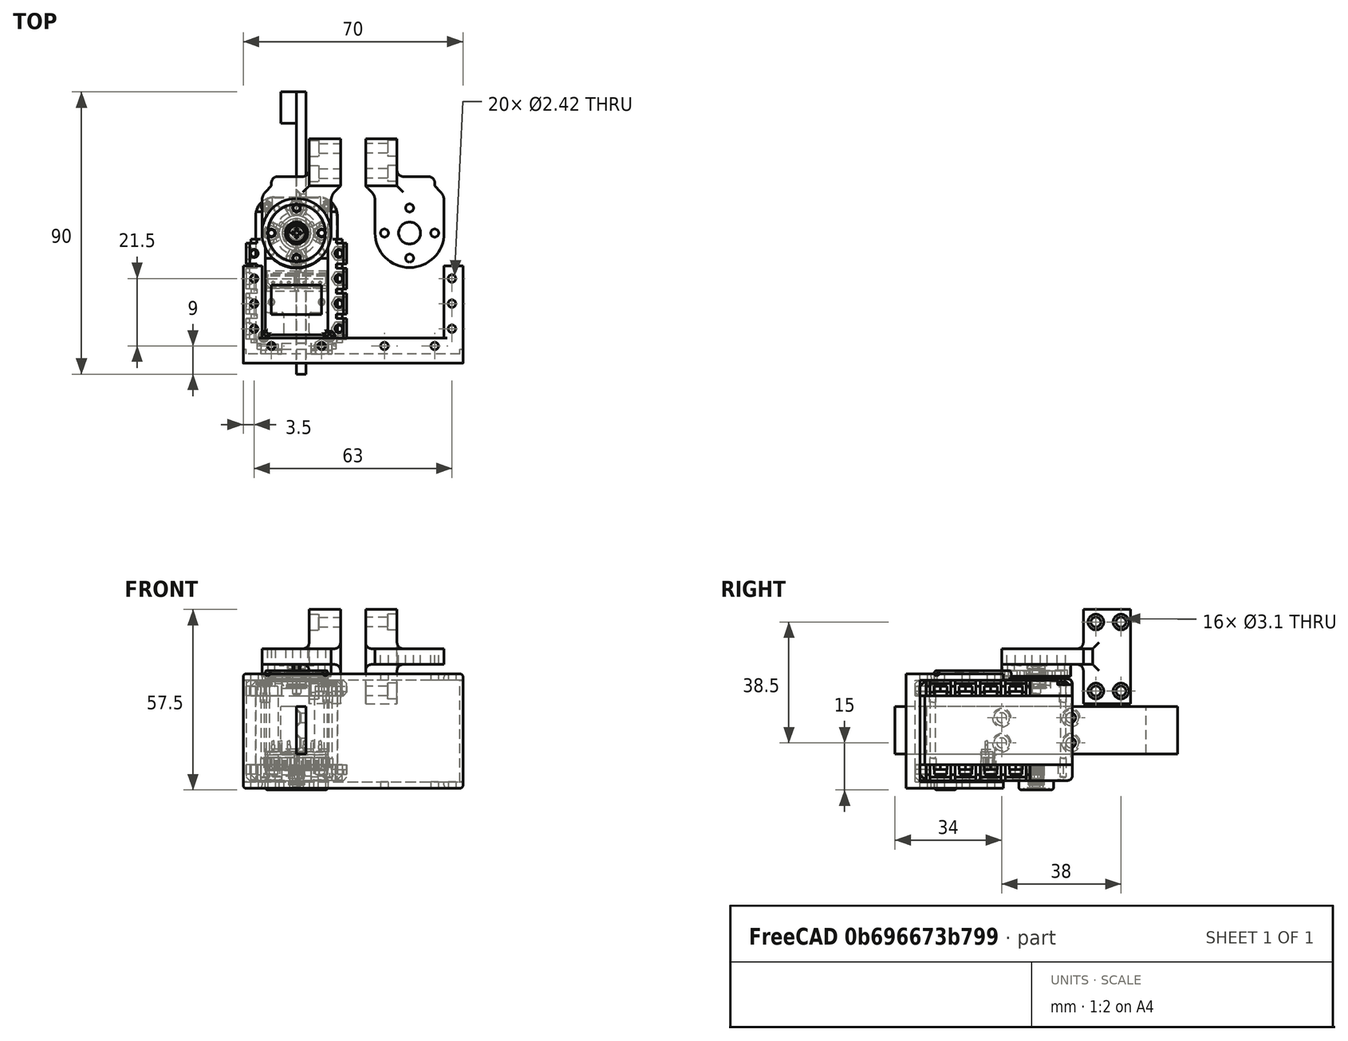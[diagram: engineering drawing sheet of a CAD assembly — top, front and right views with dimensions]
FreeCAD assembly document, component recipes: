
FREECAD ASSEMBLY — COMPONENT RECIPES ("Unnamed")

This assembly document has 8 components, labeled P0..P7 below (a component is one placed body or linked part). 6 of them carry a construction recipe — the FreeCAD feature program that regenerates the part from scratch, quoted from this document or its linked companion documents; the rest are supplied as boundary geometry only. No exploded tour is included for this assembly.
COMPONENT P0 — geometry summary ("ASM0001_ASM002"; no construction recipe available for this part):
  bounding box: 50.0 x 40.0 x 32.0 mm
  tessellated surface: 148,570 triangles
  volume: 42792 mm^3 (67% of its bounding box)
COMPONENT P1 — geometry summary ("ASM0001_ASM003"; no construction recipe available for this part):
  bounding box: 50.0 x 40.0 x 32.0 mm
  tessellated surface: 148,570 triangles
  volume: 42792 mm^3 (67% of its bounding box)
COMPONENT P2 — recipe-attached ("Body006", modeled in this document).
Construction recipe (the document's own serialized feature program — sketch geometry with constraints, then the solid features built on it; lengths are millimeters unless a unit is written):

FEATURE [PartDesign::ShapeBinder] CopyPart__Feature
  TraceSupport = false
FEATURE [Sketcher::SketchObject] Sketch012
  ArcFitTolerance = 1e-06
  AttachmentSupport = -> [CopyPart__Feature]
  ExternalTypes = [0]
  FullyConstrained = true
  MakeInternals = false
  MapMode = 5
  Placement = pos=(0,-38.5,0) rot=(1,0,0;1.5708rad)
  _ExternalGeoVersion = 1
  sketch-geometry (4):
    g0: LineSegment StartX=-17 StartY=18 StartZ=0 EndX=-17 EndY=-18.5 EndZ=0
    g1: LineSegment StartX=-17 StartY=-18.5 StartZ=0 EndX=53 EndY=-18.5 EndZ=0
    g2: LineSegment StartX=53 StartY=-18.5 StartZ=0 EndX=53 EndY=18 EndZ=0
    g3: LineSegment StartX=53 StartY=18 StartZ=0 EndX=-17 EndY=18 EndZ=0
  constraints (12):
    c: Coincident(g0,g1)
    c: Coincident(g1,g2)
    c: Coincident(g2,g3)
    c: Coincident(g3,g0)
    c: Vertical(g0)
    c: Vertical(g2)
    c: Horizontal(g1)
    c: Horizontal(g3)
    c: DistanceY(g0,g0) = 36.5
    c: Distance(g-2,g0) = 17
    c: DistanceX(g1,g1) = 70
    c: Distance(g-1,g3) = 18
FEATURE [PartDesign::Pad] Pad006
  Direction = (0,-1,2e-16)
  Length = 3
  Length2 = 10
  Profile = -> Sketch012
  ReferenceAxis = -> Sketch012 [N_Axis]
  Refine = true
  SideType = 0
  Suppressed = false
  Type = 0
  Type2 = 0
FEATURE [Sketcher::SketchObject] Sketch013
  ArcFitTolerance = 1e-06
  AttachmentSupport = -> [Pad006]
  ExternalTypes = [0]
  FullyConstrained = true
  MakeInternals = false
  MapMode = 5
  Placement = pos=(0,-38.5,1.5e-14) rot=(0,0.707107,0.707107;3.14159rad)
  _ExternalGeoVersion = 1
  sketch-geometry (4):
    g0: LineSegment StartX=17 StartY=18 StartZ=0 EndX=-53 EndY=18 EndZ=0
    g1: LineSegment StartX=-53 StartY=18 StartZ=0 EndX=-53 EndY=16 EndZ=0
    g2: LineSegment StartX=-53 StartY=16 StartZ=0 EndX=17 EndY=16 EndZ=0
    g3: LineSegment StartX=17 StartY=16 StartZ=0 EndX=17 EndY=18 EndZ=0
  constraints (12):
    c: Coincident(g0,g1)
    c: Coincident(g1,g2)
    c: Coincident(g2,g3)
    c: Coincident(g3,g0)
    c: Horizontal(g0)
    c: Horizontal(g2)
    c: Vertical(g1)
    c: Vertical(g3)
    c: Distance(g1,g3) = 70
    c: Distance(g0,g2) = 2
    c: Distance(g-1,g2) = 16
    c: Distance(g-2,g3) = 17
FEATURE [PartDesign::Pad] Pad007
  BaseFeature = -> Pad006
  Direction = (0,1,-2e-16)
  Length = 5
  Length2 = 10
  Profile = -> Sketch013
  ReferenceAxis = -> Sketch013 [N_Axis]
  Refine = true
  SideType = 0
  Suppressed = false
  Type = 0
  Type2 = 0
FEATURE [Sketcher::SketchObject] Sketch014
  ArcFitTolerance = 1e-06
  AttachmentSupport = -> [Pad007]
  ExternalTypes = [0]
  FullyConstrained = true
  MakeInternals = false
  MapMode = 5
  Placement = pos=(0,-38.5,1.5e-14) rot=(0,0.707107,0.707107;3.14159rad)
  _ExternalGeoVersion = 1
  sketch-geometry (4):
    g0: LineSegment StartX=17 StartY=-18.5 StartZ=0 EndX=17 EndY=-16.5 EndZ=0
    g1: LineSegment StartX=17 StartY=-16.5 StartZ=0 EndX=-53 EndY=-16.5 EndZ=0
    g2: LineSegment StartX=-53 StartY=-16.5 StartZ=0 EndX=-53 EndY=-18.5 EndZ=0
    g3: LineSegment StartX=-53 StartY=-18.5 StartZ=0 EndX=17 EndY=-18.5 EndZ=0
  constraints (12):
    c: Coincident(g0,g1)
    c: Coincident(g1,g2)
    c: Coincident(g2,g3)
    c: Coincident(g3,g0)
    c: Vertical(g0)
    c: Vertical(g2)
    c: Horizontal(g1)
    c: Horizontal(g3)
    c: Distance(g0,g2) = 70
    c: Distance(g1,g3) = 2
    c: Distance(g-2,g0) = 17
    c: Distance(g-1,g3) = 18.5
FEATURE [PartDesign::Pad] Pad008
  BaseFeature = -> Pad007
  Direction = (0,1,-2e-16)
  Length = 5
  Length2 = 10
  Profile = -> Sketch014
  ReferenceAxis = -> Sketch014 [N_Axis]
  Refine = true
  SideType = 0
  Suppressed = false
  Type = 0
  Type2 = 0
FEATURE [Sketcher::SketchObject] Sketch015
  ArcFitTolerance = 1e-06
  AttachmentSupport = -> [Pad008]
  ExternalTypes = [0,0]
  FullyConstrained = true
  MakeInternals = false
  MapMode = 5
  Placement = pos=(0,-33.5,1.19e-13) rot=(0,0.707107,0.707107;3.14159rad)
  _ExternalGeoVersion = 1
  sketch-geometry (16):
    g0: LineSegment StartX=17 StartY=16 StartZ=0 EndX=17 EndY=18 EndZ=0
    g1: LineSegment StartX=17 StartY=18 StartZ=0 EndX=11 EndY=18 EndZ=0
    g2: LineSegment StartX=11 StartY=18 StartZ=0 EndX=11 EndY=16 EndZ=0
    g3: LineSegment StartX=11 StartY=16 StartZ=0 EndX=17 EndY=16 EndZ=0
    g4: LineSegment StartX=-53 StartY=16 StartZ=0 EndX=-47 EndY=16 EndZ=0
    g5: LineSegment StartX=-47 StartY=16 StartZ=0 EndX=-47 EndY=18 EndZ=0
    g6: LineSegment StartX=-47 StartY=18 StartZ=0 EndX=-53 EndY=18 EndZ=0
    g7: LineSegment StartX=-53 StartY=18 StartZ=0 EndX=-53 EndY=16 EndZ=0
    g8: LineSegment StartX=-53 StartY=-16.5 StartZ=0 EndX=-53 EndY=-18.5 EndZ=0
    g9: LineSegment StartX=-53 StartY=-18.5 StartZ=0 EndX=-47 EndY=-18.5 EndZ=0
    g10: LineSegment StartX=-47 StartY=-18.5 StartZ=0 EndX=-47 EndY=-16.5 EndZ=0
    g11: LineSegment StartX=-47 StartY=-16.5 StartZ=0 EndX=-53 EndY=-16.5 EndZ=0
    g12: LineSegment StartX=17 StartY=-16.5 StartZ=0 EndX=11 EndY=-16.5 EndZ=0
    g13: LineSegment StartX=11 StartY=-16.5 StartZ=0 EndX=11 EndY=-18.5 EndZ=0
    g14: LineSegment StartX=11 StartY=-18.5 StartZ=0 EndX=17 EndY=-18.5 EndZ=0
    g15: LineSegment StartX=17 StartY=-18.5 StartZ=0 EndX=17 EndY=-16.5 EndZ=0
  constraints (48):
    c: Coincident(g0,g1)
    c: Coincident(g1,g2)
    c: Coincident(g2,g3)
    c: Coincident(g3,g0)
    c: Vertical(g0)
    c: Vertical(g2)
    c: Horizontal(g1)
    c: Horizontal(g3)
    c: Distance(g0,g2) = 6
    c: Distance(g1,g3) = 2
    c: Distance(g-1,g3) = 16
    c: Distance(g-2,g0) = 17
    c: Coincident(g4,g5)
    c: Coincident(g5,g6)
    c: Coincident(g6,g7)
    c: Coincident(g7,g4)
    c: Horizontal(g4)
    c: Horizontal(g6)
    c: Vertical(g5)
    c: Vertical(g7)
    c: Distance(g-1,g4) = 16
    c: Distance(g7,g7) = 2
    c: Distance(g-2,g7) = 53
    c: Distance(g6,g6) = 6
    c: Coincident(g8,g9)
    c: Coincident(g9,g10)
    c: Coincident(g10,g11)
    c: Coincident(g11,g8)
    c: Vertical(g8)
    c: Vertical(g10)
    c: Horizontal(g9)
    c: Horizontal(g11)
    c: Coincident(g12,g13)
    c: Coincident(g13,g14)
    c: Coincident(g14,g15)
    c: Coincident(g15,g12)
    c: Horizontal(g12)
    c: Horizontal(g14)
    c: Vertical(g13)
    c: Vertical(g15)
    c: Distance(g-2,g15) = 17
    c: Distance(g-1,g12) = 16.5
    c: Distance(g13,g13) = 2
    c: Distance(g14,g14) = 6
    c: Distance(g-1,g11) = 16.5
    c: Distance(g-2,g8) = 53
    c: Distance(g9,g9) = 6
    c: Distance(g10,g10) = 2
FEATURE [PartDesign::Pad] Pad009
  BaseFeature = -> Pad008
  Direction = (0,1,-3.6e-15)
  Length = 23
  Length2 = 10
  Profile = -> Sketch015
  ReferenceAxis = -> Sketch015 [N_Axis]
  Refine = true
  SideType = 0
  Suppressed = false
  Type = 0
  Type2 = 0
FEATURE [Sketcher::SketchObject] Sketch016
  ArcFitTolerance = 1e-06
  AttachmentSupport = -> [Pad009]
  ExternalTypes = [0,0]
  FullyConstrained = true
  MakeInternals = false
  MapMode = 5
  Placement = pos=(0,-38.5,1.5e-14) rot=(0,0.707107,0.707107;3.14159rad)
  _ExternalGeoVersion = 1
  sketch-geometry (8):
    g0: LineSegment StartX=-53 StartY=16 StartZ=0 EndX=-53 EndY=-16.5 EndZ=0
    g1: LineSegment StartX=-53 StartY=-16.5 StartZ=0 EndX=-52 EndY=-16.5 EndZ=0
    g2: LineSegment StartX=-52 StartY=-16.5 StartZ=0 EndX=-52 EndY=16 EndZ=0
    g3: LineSegment StartX=-52 StartY=16 StartZ=0 EndX=-53 EndY=16 EndZ=0
    g4: LineSegment StartX=17 StartY=16 StartZ=0 EndX=16 EndY=16 EndZ=0
    g5: LineSegment StartX=16 StartY=16 StartZ=0 EndX=16 EndY=-16.5 EndZ=0
    g6: LineSegment StartX=16 StartY=-16.5 StartZ=0 EndX=17 EndY=-16.5 EndZ=0
    g7: LineSegment StartX=17 StartY=-16.5 StartZ=0 EndX=17 EndY=16 EndZ=0
  constraints (24):
    c: Coincident(g0,g1)
    c: Coincident(g1,g2)
    c: Coincident(g2,g3)
    c: Coincident(g3,g0)
    c: Vertical(g0)
    c: Vertical(g2)
    c: Horizontal(g1)
    c: Horizontal(g3)
    c: Distance(g0,g2) = 1
    c: Distance(g1,g3) = 32.5
    c: Distance(g-1,g3) = 16
    c: Distance(g-2,g0) = 53
    c: Coincident(g4,g5)
    c: Coincident(g5,g6)
    c: Coincident(g6,g7)
    c: Coincident(g7,g4)
    c: Horizontal(g4)
    c: Horizontal(g6)
    c: Vertical(g5)
    c: Vertical(g7)
    c: Distance(g-2,g7) = 17
    c: Distance(g-1,g4) = 16
    c: Distance(g7,g7) = 32.5
    c: Distance(g6,g6) = 1
FEATURE [PartDesign::Pad] Pad010
  BaseFeature = -> Pad009
  Direction = (0,1,-2e-16)
  Length = 1.5
  Length2 = 10
  Profile = -> Sketch016
  ReferenceAxis = -> Sketch016 [N_Axis]
  Refine = true
  SideType = 0
  Suppressed = false
  Type = 0
  Type2 = 0
FEATURE [PartDesign::Fillet] Fillet008
  Base = -> Pad010 [Edge47,Edge45,Edge20,Edge18,Edge5,Edge23,Edge41,Edge43]
  BaseFeature = -> Pad010
  Radius = 1
  Refine = true
  SupportTransform = false
  Suppressed = false
  UseAllEdges = false
FEATURE [Sketcher::SketchObject] Sketch017
  ArcFitTolerance = 1e-06
  AttachmentSupport = -> [Fillet008]
  ExternalTypes = [0]
  FullyConstrained = true
  MakeInternals = false
  MapMode = 5
  Placement = pos=(0,-1.22e-14,18) rot=(0,0,1;0rad)
  _ExternalGeoVersion = 1
  sketch-geometry (10):
    g0: Circle CenterX=-13.5 CenterY=-14.5 CenterZ=0 NormalX=0 NormalY=0 NormalZ=1 AngleXU=0 Radius=1.1
    g1: Circle CenterX=-13.5 CenterY=-22.5 CenterZ=0 NormalX=0 NormalY=0 NormalZ=1 AngleXU=0 Radius=1.1
    g2: Circle CenterX=-13.5 CenterY=-30.5 CenterZ=0 NormalX=0 NormalY=0 NormalZ=1 AngleXU=0 Radius=1.1
    g3: Circle CenterX=49.5 CenterY=-14.5 CenterZ=0 NormalX=0 NormalY=0 NormalZ=1 AngleXU=0 Radius=1.1
    g4: Circle CenterX=49.5 CenterY=-22.5 CenterZ=0 NormalX=0 NormalY=0 NormalZ=1 AngleXU=0 Radius=1.1
    g5: Circle CenterX=49.5 CenterY=-30.5 CenterZ=0 NormalX=0 NormalY=0 NormalZ=1 AngleXU=0 Radius=1.1
    g6: Circle CenterX=-8 CenterY=-36 CenterZ=0 NormalX=0 NormalY=0 NormalZ=1 AngleXU=0 Radius=1.1
    g7: Circle CenterX=8 CenterY=-36 CenterZ=0 NormalX=0 NormalY=0 NormalZ=1 AngleXU=0 Radius=1.1
    g8: Circle CenterX=44 CenterY=-36 CenterZ=0 NormalX=0 NormalY=0 NormalZ=1 AngleXU=0 Radius=1.1
    g9: Circle CenterX=28 CenterY=-36 CenterZ=0 NormalX=0 NormalY=0 NormalZ=1 AngleXU=0 Radius=1.1
  constraints (30):
    c: Diameter(g0) = 2.2
    c: Equal(g0,g1)
    c: Equal(g2,g1)
    c: Distance(g0,g-2) = 13.5
    c: DistanceY(g0,g-1) = 14.5
    c: Distance(g1,g0) = 8
    c: Distance(g1,g-2) = 13.5
    c: Distance(g2,g1) = 8
    c: Distance(g2,g-2) = 13.5
    c: Diameter(g3) = 2.2
    c: DistanceX(g-1,g3) = 49.5
    c: DistanceY(g3,g-1) = 14.5
    c: Equal(g3,g4)
    c: Equal(g4,g5)
    c: Distance(g4,g3) = 8
    c: Distance(g5,g4) = 8
    c: Distance(g4,g-2) = 49.5
    c: Distance(g5,g-2) = 49.5
    c: Equal(g2,g6)
    c: Distance(g6,g-2) = 8
    c: DistanceY(g6,g-1) = 36
    c: Equal(g7,g6)
    c: DistanceX(g6,g7) = 16
    c: Distance(g7,g-1) = 36
    c: Equal(g9,g5)
    c: Equal(g8,g5)
    c: DistanceX(g9,g8) = 16
    c: Distance(g9,g-1) = 36
    c: Distance(g8,g-1) = 36
    c: Distance(g9,g-2) = 28
FEATURE [PartDesign::Hole] Hole006
  BaseFeature = -> Fillet008
  BaseProfileType = 7
  CustomThreadClearance = 0
  Depth = 40
  DepthType = 0
  Diameter = 2.42
  DrillForDepth = false
  DrillPoint = 1
  DrillPointAngle = 118
  HoleCutCountersinkAngle = 90
  HoleCutCustomValues = false
  HoleCutDepth = 0
  HoleCutDiameter = 0
  HoleCutType = 0
  ModelThread = false
  Profile = -> Sketch017
  Refine = true
  Suppressed = false
  Tapered = false
  TaperedAngle = 90
  ThreadClass = 0
  ThreadDepth = 40
  ThreadDepthType = 0
  ThreadDiameter = 2.2
  ThreadDirection = 0
  ThreadFit = 0
  ThreadSize = 7
  ThreadType = 1
  Threaded = false
  UseCustomThreadClearance = false
FEATURE [PartDesign::Body] Body002
  AllowCompound = true
  Group = -> [CopyPart__Feature,Sketch012,Pad006,Sketch013,Pad007,Sketch014,Pad008,Sketch015,Pad009,Sketch016,Pad010,Fillet008,Sketch017,Hole006]
  Origin = -> Origin012
  Tip = -> Hole006
COMPONENT P3 — recipe-attached ("Body007", modeled in this document).
Construction recipe (the document's own serialized feature program — sketch geometry with constraints, then the solid features built on it; lengths are millimeters unless a unit is written):

FEATURE [PartDesign::ShapeBinder] CopyPart__Feature009
  Placement = pos=(0,0,19.16) rot=(0,0,1;1.5708rad)
  TraceSupport = false
FEATURE [Sketcher::SketchObject] Sketch
  ArcFitTolerance = 1e-06
  AttachmentSupport = -> [CopyPart__Feature009]
  ExternalTypes = [0]
  FullyConstrained = true
  MakeInternals = false
  MapMode = 5
  Placement = pos=(0,0,21) rot=(0,0,1;1.5708rad)
  _ExternalGeoVersion = 1
  sketch-geometry (4):
    g0: LineSegment StartX=-2e-15 StartY=-11 StartZ=0 EndX=12 EndY=-11 EndZ=0
    g1: LineSegment StartX=12 StartY=-11 StartZ=0 EndX=12 EndY=11 EndZ=0
    g2: LineSegment StartX=12 StartY=11 StartZ=0 EndX=-3.6e-15 EndY=11 EndZ=0
    g3: ArcOfCircle CenterX=0 CenterY=5e-16 CenterZ=0 NormalX=0 NormalY=0 NormalZ=1 AngleXU=0 Radius=11 StartAngle=1.5708 EndAngle=4.71239
  constraints (12):
    c: Coincident(g0,g1)
    c: Coincident(g1,g2)
    c: Horizontal(g0)
    c: Horizontal(g2)
    c: Vertical(g1)
    c: Distance(g1,g0) = 12
    c: Distance(g0,g2) = 22
    c: PointOnObject(g0,g-2)
    c: Distance(g-1,g0) = 11
    c: Tangent(g0,g3) = -1.5708
    c: Coincident(g3,g2)
    c: Angle(g3) = 3.14159
FEATURE [PartDesign::Pad] Pad
  Direction = (0,0,1)
  Length = 5
  Length2 = 10
  Placement = pos=(0,0,19.16) rot=(0,0,1;1.5708rad)
  Profile = -> Sketch
  ReferenceAxis = -> Sketch [N_Axis]
  Refine = true
  SideType = 0
  Suppressed = false
  Type = 0
  Type2 = 0
FEATURE [Sketcher::SketchObject] Sketch001
  ArcFitTolerance = 1e-06
  AttachmentSupport = -> [Pad]
  ExternalTypes = [0]
  FullyConstrained = true
  MakeInternals = false
  MapMode = 5
  Placement = pos=(0,0,26) rot=(0,0,1;1.5708rad)
  _ExternalGeoVersion = 1
  sketch-geometry (1):
    g0: Circle CenterX=-8 CenterY=0 CenterZ=0 NormalX=0 NormalY=0 NormalZ=1 AngleXU=0 Radius=1.1
  constraints (3):
    c: Diameter(g0) = 2.2
    c: PointOnObject(g0,g-1)
    c: Distance(g0,g-2) = 8
FEATURE [PartDesign::Hole] Hole
  BaseFeature = -> Pad
  BaseProfileType = 7
  CustomThreadClearance = 0
  Depth = 5
  DepthType = 0
  Diameter = 2.552
  DrillForDepth = false
  DrillPoint = 1
  DrillPointAngle = 118
  HoleCutCountersinkAngle = 90
  HoleCutCustomValues = false
  HoleCutDepth = 0
  HoleCutDiameter = 0
  HoleCutType = 0
  ModelThread = false
  Placement = pos=(0,0,19.16) rot=(0,0,1;1.5708rad)
  Profile = -> Sketch001
  Refine = true
  Suppressed = false
  Tapered = false
  TaperedAngle = 90
  ThreadClass = 0
  ThreadDepth = 5
  ThreadDepthType = 0
  ThreadDiameter = 2.2
  ThreadDirection = 0
  ThreadFit = 2
  ThreadSize = 7
  ThreadType = 1
  Threaded = false
  UseCustomThreadClearance = false
FEATURE [PartDesign::PolarPattern] PolarPattern
  Angle = 360
  Axis = -> Sketch001 [N_Axis]
  BaseFeature = -> Hole
  Mode = 0
  Occurrences = 4
  Offset = 120
  Originals = -> [Hole]
  Placement = pos=(0,0,19.16) rot=(0,0,1;1.5708rad)
  Refine = true
  SpacingPattern = [0]
  Spacings = [-1,-1,-1]
  Suppressed = false
  TransformMode = 0
FEATURE [Sketcher::SketchObject] Sketch002
  ArcFitTolerance = 1e-06
  AttachmentSupport = -> [PolarPattern]
  ExternalTypes = [0]
  FullyConstrained = true
  MakeInternals = false
  MapMode = 5
  Placement = pos=(0,0,26) rot=(0,0,1;1.5708rad)
  _ExternalGeoVersion = 1
  sketch-geometry (1):
    g0: Circle CenterX=0 CenterY=0 CenterZ=0 NormalX=0 NormalY=0 NormalZ=1 AngleXU=0 Radius=3
  constraints (2):
    c: Diameter(g0) = 6
    c: Coincident(g0,g-1)
FEATURE [PartDesign::Hole] Hole001
  BaseFeature = -> PolarPattern
  BaseProfileType = 7
  CustomThreadClearance = 0
  Depth = 5
  DepthType = 0
  Diameter = 7
  DrillForDepth = false
  DrillPoint = 1
  DrillPointAngle = 118
  HoleCutCountersinkAngle = 90
  HoleCutCustomValues = false
  HoleCutDepth = 0
  HoleCutDiameter = 0
  HoleCutType = 0
  ModelThread = false
  Placement = pos=(0,0,19.16) rot=(0,0,1;1.5708rad)
  Profile = -> Sketch002
  Refine = true
  Suppressed = false
  Tapered = false
  TaperedAngle = 90
  ThreadClass = 0
  ThreadDepth = 5
  ThreadDepthType = 0
  ThreadDiameter = 6
  ThreadDirection = 0
  ThreadFit = 2
  ThreadSize = 14
  ThreadType = 1
  Threaded = false
  UseCustomThreadClearance = false
FEATURE [Sketcher::SketchObject] Sketch018
  ArcFitTolerance = 1e-06
  AttachmentSupport = -> [Hole001]
  ExternalTypes = [0]
  FullyConstrained = true
  MakeInternals = false
  MapMode = 5
  Placement = pos=(0,0,26) rot=(0,0,1;1.5708rad)
  _ExternalGeoVersion = 1
  sketch-geometry (4):
    g0: LineSegment StartX=12 StartY=11 StartZ=0 EndX=15 EndY=8.00374 EndZ=0
    g1: LineSegment StartX=15 StartY=8.00374 StartZ=0 EndX=15 EndY=-13.9963 EndZ=0
    g2: LineSegment StartX=15 StartY=-13.9963 StartZ=0 EndX=12 EndY=-11 EndZ=0
    g3: LineSegment StartX=12 StartY=11 StartZ=0 EndX=12 EndY=-11 EndZ=0
  constraints (12):
    c: Coincident(g0,g1)
    c: Vertical(g1)
    c: Coincident(g1,g2)
    c: Coincident(g0,g3)
    c: Coincident(g3,g2)
    c: Vertical(g3)
    c: Distance(g1,g1) = 22
    c: Distance(g0,g0) = 4.24
    c: Equal(g1,g3)
    c: Distance(g-2,g1) = 15
    c: Distance(g-2,g3) = 12
    c: Distance(g0,g-1) = 11
FEATURE [PartDesign::Pad] Pad011
  BaseFeature = -> Hole001
  Direction = (0,0,1)
  Length = 5
  Length2 = 10
  Placement = pos=(0,0,19.16) rot=(0,0,1;1.5708rad)
  Profile = -> Sketch018
  ReferenceAxis = -> Sketch018 [N_Axis]
  Refine = true
  Reversed = true
  SideType = 0
  Suppressed = false
  Type = 0
  Type2 = 0
FEATURE [Sketcher::SketchObject] Sketch019
  ArcFitTolerance = 1e-06
  AttachmentSupport = -> [Pad011]
  ExternalTypes = [0,0,0]
  FullyConstrained = true
  MakeInternals = false
  MapMode = 5
  Placement = pos=(0,0,26) rot=(0,0,1;1.5708rad)
  _ExternalGeoVersion = 1
  sketch-geometry (4):
    g0: LineSegment StartX=15 StartY=8 StartZ=0 EndX=15 EndY=-14 EndZ=0
    g1: LineSegment StartX=15 StartY=-14 StartZ=0 EndX=18 EndY=-14 EndZ=0
    g2: LineSegment StartX=18 StartY=-14 StartZ=0 EndX=18 EndY=8 EndZ=0
    g3: LineSegment StartX=18 StartY=8 StartZ=0 EndX=15 EndY=8 EndZ=0
  constraints (12):
    c: Coincident(g0,g1)
    c: Coincident(g1,g2)
    c: Coincident(g2,g3)
    c: Coincident(g3,g0)
    c: Vertical(g0)
    c: Vertical(g2)
    c: Horizontal(g1)
    c: Horizontal(g3)
    c: Distance(g0,g2) = 3
    c: Distance(g1,g3) = 22
    c: Distance(g-2,g2) = 18
    c: Distance(g1,g-1) = 14
FEATURE [PartDesign::Pad] Pad012
  BaseFeature = -> Pad011
  Direction = (0,0,1)
  Length = 5
  Length2 = 10
  Placement = pos=(0,0,19.16) rot=(0,0,1;1.5708rad)
  Profile = -> Sketch019
  ReferenceAxis = -> Sketch019 [N_Axis]
  Refine = true
  Reversed = true
  SideType = 0
  Suppressed = false
  Type = 0
  Type2 = 0
FEATURE [Sketcher::SketchObject] Sketch020
  ArcFitTolerance = 1e-06
  AttachmentSupport = -> [Pad012]
  ExternalTypes = [0]
  FullyConstrained = true
  MakeInternals = false
  MapMode = 5
  Placement = pos=(14,-4.7e-15,19.16) rot=(0.57735,0.57735,0.57735;2.0944rad)
  _ExternalGeoVersion = 1
  sketch-geometry (4):
    g0: LineSegment StartX=15 StartY=19.34 StartZ=0 EndX=15 EndY=-10.66 EndZ=0
    g1: LineSegment StartX=15 StartY=-10.66 StartZ=0 EndX=30 EndY=-10.66 EndZ=0
    g2: LineSegment StartX=30 StartY=-10.66 StartZ=0 EndX=30 EndY=19.34 EndZ=0
    g3: LineSegment StartX=30 StartY=19.34 StartZ=0 EndX=15 EndY=19.34 EndZ=0
  constraints (12):
    c: Coincident(g0,g1)
    c: Coincident(g1,g2)
    c: Coincident(g2,g3)
    c: Coincident(g3,g0)
    c: Vertical(g0)
    c: Vertical(g2)
    c: Horizontal(g1)
    c: Horizontal(g3)
    c: Distance(g0,g2) = 15
    c: Distance(g1,g3) = 30
    c: Distance(g-1,g1) = 10.66
    c: Distance(g-2,g0) = 15
FEATURE [PartDesign::Pad] Pad013
  BaseFeature = -> Pad012
  Direction = (1,0,0)
  Length = 10
  Length2 = 10
  Placement = pos=(0,0,19.16) rot=(0,0,1;1.5708rad)
  Profile = -> Sketch020
  ReferenceAxis = -> Sketch020 [N_Axis]
  Refine = true
  Reversed = true
  SideType = 0
  Suppressed = false
  Type = 0
  Type2 = 0
FEATURE [PartDesign::Fillet] Fillet
  Base = -> Pad013 [Edge42,Edge40,Edge28,Edge12]
  BaseFeature = -> Pad013
  Placement = pos=(0,0,19.16) rot=(0,0,1;1.5708rad)
  Radius = 2
  Refine = true
  SupportTransform = false
  Suppressed = false
  UseAllEdges = false
FEATURE [PartDesign::Fillet] Fillet009
  Base = -> Fillet [Edge31,Edge29,Edge6,Edge4]
  BaseFeature = -> Fillet
  Placement = pos=(0,0,19.16) rot=(0,0,1;1.5708rad)
  Radius = 2
  Refine = true
  SupportTransform = false
  Suppressed = false
  UseAllEdges = false
FEATURE [PartDesign::Fillet] Fillet010
  Base = -> Fillet009 [Edge29,Edge19]
  BaseFeature = -> Fillet009
  Placement = pos=(0,0,19.16) rot=(0,0,1;1.5708rad)
  Radius = 4
  Refine = true
  SupportTransform = false
  Suppressed = false
  UseAllEdges = false
FEATURE [Sketcher::SketchObject] Sketch021
  ArcFitTolerance = 1e-06
  AttachmentSupport = -> [Fillet010]
  ExternalTypes = [0,0,0]
  FullyConstrained = true
  MakeInternals = false
  MapMode = 5
  Placement = pos=(4,-4e-16,19.16) rot=(0.57735,-0.57735,-0.57735;2.0944rad)
  _ExternalGeoVersion = 1
  sketch-geometry (4):
    g0: Circle CenterX=-19 CenterY=15.34 CenterZ=0 NormalX=0 NormalY=0 NormalZ=1 AngleXU=0 Radius=1.1
    g1: Circle CenterX=-27 CenterY=15.34 CenterZ=0 NormalX=0 NormalY=0 NormalZ=1 AngleXU=0 Radius=1.1
    g2: Circle CenterX=-19 CenterY=-6.66 CenterZ=0 NormalX=0 NormalY=0 NormalZ=1 AngleXU=0 Radius=1.1
    g3: Circle CenterX=-27 CenterY=-6.66 CenterZ=0 NormalX=0 NormalY=0 NormalZ=1 AngleXU=0 Radius=1.1
  constraints (12):
    c: Diameter(g0) = 2.2
    c: Equal(g1,g0)
    c: Equal(g3,g1)
    c: Equal(g2,g3)
    c: DistanceX(g1,g0) = 8
    c: DistanceX(g3,g2) = 8
    c: Distance(g0,g-1) = 15.34
    c: Distance(g0,g-2) = 19
    c: Distance(g1,g-1) = 15.34
    c: Distance(g2,g-2) = 19
    c: Distance(g2,g-1) = 6.66
    c: Distance(g3,g-1) = 6.66
FEATURE [PartDesign::Hole] Hole007
  BaseFeature = -> Fillet010
  BaseProfileType = 7
  CustomThreadClearance = 0
  Depth = 10
  DepthType = 0
  Diameter = 3.1
  DrillForDepth = false
  DrillPoint = 0
  DrillPointAngle = 118
  HoleCutCountersinkAngle = 90
  HoleCutCustomValues = false
  HoleCutDepth = 3
  HoleCutDiameter = 5
  HoleCutType = 1
  ModelThread = false
  Placement = pos=(0,0,19.16) rot=(0,0,1;1.5708rad)
  Profile = -> Sketch021
  Refine = true
  Suppressed = false
  Tapered = false
  TaperedAngle = 90
  ThreadClass = 0
  ThreadDepth = 10
  ThreadDepthType = 0
  ThreadDiameter = 2.5
  ThreadDirection = 0
  ThreadFit = 2
  ThreadSize = 8
  ThreadType = 1
  Threaded = false
  UseCustomThreadClearance = false
FEATURE [PartDesign::Body] Body
  AllowCompound = true
  Group = -> [CopyPart__Feature009,Sketch,Pad,Sketch001,Hole,PolarPattern,Sketch002,Hole001,Sketch018,Pad011,Sketch019,Pad012,Sketch020,Pad013,Fillet,Fillet009,Fillet010,Sketch021,Hole007]
  Origin = -> Origin004
  Tip = -> Hole007
COMPONENT P4 — same part as P3; its construction recipe is shown at P3.
COMPONENT P5 — recipe-attached ("Body009", modeled in this document).
Construction recipe (the document's own serialized feature program — sketch geometry with constraints, then the solid features built on it; lengths are millimeters unless a unit is written):

FEATURE [Sketcher::SketchObject] Sketch032
  ArcFitTolerance = 1e-06
  AttachmentSupport = -> [Origin018]
  ExternalTypes = [0]
  FullyConstrained = true
  MakeInternals = false
  MapMode = 5
  Placement = pos=(0,0,0) rot=(0.57735,0.57735,0.57735;2.0944rad)
  _ExternalGeoVersion = 1
  sketch-geometry (5):
    g0: LineSegment StartX=-45 StartY=-7.5 StartZ=0 EndX=45 EndY=-7.5 EndZ=0
    g1: LineSegment StartX=45 StartY=-7.5 StartZ=0 EndX=45 EndY=7.5 EndZ=0
    g2: LineSegment StartX=45 StartY=7.5 StartZ=0 EndX=-45 EndY=7.5 EndZ=0
    g3: LineSegment StartX=-45 StartY=7.5 StartZ=0 EndX=-45 EndY=-7.5 EndZ=0
    g4: GeomPoint [constr] X=0 Y=0 Z=0
  constraints (12):
    c: Coincident(g0,g1)
    c: Coincident(g1,g2)
    c: Coincident(g2,g3)
    c: Coincident(g3,g0)
    c: Horizontal(g0)
    c: Horizontal(g2)
    c: Vertical(g1)
    c: Vertical(g3)
    c: Symmetric(g2,g0,g4)
    c: Distance(g1,g3) = 90
    c: Distance(g0,g2) = 15
    c: Coincident(g4,g-1)
FEATURE [PartDesign::Pad] Pad020
  Direction = (1,0,0)
  Length = 3
  Length2 = 10
  Profile = -> Sketch032
  ReferenceAxis = -> Sketch032 [N_Axis]
  Refine = true
  SideType = 0
  Suppressed = false
  Type = 0
  Type2 = 0
FEATURE [Sketcher::SketchObject] Sketch033
  ArcFitTolerance = 1e-06
  AttachmentSupport = -> [Pad020]
  ExternalTypes = [0]
  FullyConstrained = true
  MakeInternals = false
  MapMode = 5
  Placement = pos=(0,0,0) rot=(0.57735,-0.57735,-0.57735;2.0944rad)
  _ExternalGeoVersion = 1
  sketch-geometry (4):
    g0: Circle CenterX=-11 CenterY=4 CenterZ=0 NormalX=0 NormalY=0 NormalZ=1 AngleXU=0 Radius=1.25
    g1: Circle CenterX=-11 CenterY=-4 CenterZ=0 NormalX=0 NormalY=0 NormalZ=1 AngleXU=0 Radius=1.25
    g2: Circle CenterX=11 CenterY=4 CenterZ=0 NormalX=0 NormalY=0 NormalZ=1 AngleXU=0 Radius=1.25
    g3: Circle CenterX=11 CenterY=-4 CenterZ=0 NormalX=0 NormalY=0 NormalZ=1 AngleXU=0 Radius=1.25
  constraints (12):
    c: Diameter(g0) = 2.5
    c: Equal(g0,g1)
    c: Equal(g1,g3)
    c: Equal(g3,g2)
    c: Distance(g0,g-1) = 4
    c: Distance(g0,g-2) = 11
    c: Distance(g1,g-2) = 11
    c: Distance(g1,g0) = 8
    c: Distance(g2,g-2) = 11
    c: Distance(g3,g-2) = 11
    c: Distance(g3,g2) = 8
    c: Distance(g2,g-1) = 4
FEATURE [PartDesign::Hole] Hole012
  BaseFeature = -> Pad020
  BaseProfileType = 7
  CustomThreadClearance = 0
  Depth = 3
  DepthType = 0
  Diameter = 3.1
  DrillForDepth = false
  DrillPoint = 0
  DrillPointAngle = 118
  HoleCutCountersinkAngle = 90
  HoleCutCustomValues = false
  HoleCutDepth = 2.95
  HoleCutDiameter = 5.9
  HoleCutType = 2
  ModelThread = false
  Profile = -> Sketch033
  Refine = true
  Suppressed = false
  Tapered = false
  TaperedAngle = 90
  ThreadClass = 0
  ThreadDepth = 3
  ThreadDepthType = 0
  ThreadDiameter = 2.5
  ThreadDirection = 0
  ThreadFit = 2
  ThreadSize = 8
  ThreadType = 1
  Threaded = false
  UseCustomThreadClearance = false
FEATURE [Sketcher::SketchObject] Sketch034
  ArcFitTolerance = 1e-06
  AttachmentSupport = -> [Hole012]
  ExternalTypes = [0]
  FullyConstrained = true
  MakeInternals = false
  MapMode = 5
  Placement = pos=(0,0,0) rot=(0.57735,-0.57735,-0.57735;2.0944rad)
  _ExternalGeoVersion = 1
  sketch-geometry (4):
    g0: LineSegment StartX=45 StartY=7.5 StartZ=0 EndX=35 EndY=7.5 EndZ=0
    g1: LineSegment StartX=35 StartY=7.5 StartZ=0 EndX=35 EndY=-7.5 EndZ=0
    g2: LineSegment StartX=35 StartY=-7.5 StartZ=0 EndX=45 EndY=-7.5 EndZ=0
    g3: LineSegment StartX=45 StartY=-7.5 StartZ=0 EndX=45 EndY=7.5 EndZ=0
  constraints (12):
    c: Coincident(g0,g1)
    c: Coincident(g1,g2)
    c: Coincident(g2,g3)
    c: Coincident(g3,g0)
    c: Horizontal(g0)
    c: Horizontal(g2)
    c: Vertical(g1)
    c: Vertical(g3)
    c: Distance(g1,g3) = 10
    c: Distance(g0,g2) = 15
    c: Distance(g-2,g1) = 35
    c: Distance(g-1,g0) = 7.5
FEATURE [PartDesign::Pocket] Pocket
  BaseFeature = -> Hole012
  Direction = (1,0,0)
  Length = 3
  Length2 = 5
  Profile = -> Sketch034
  ReferenceAxis = -> Sketch034 [N_Axis]
  Refine = true
  SideType = 0
  Suppressed = false
  Type = 0
  Type2 = 0
FEATURE [PartDesign::Body] Body005
  AllowCompound = true
  Group = -> [Sketch032,Pad020,Sketch033,Hole012,Sketch034,Pocket]
  Origin = -> Origin018
  Tip = -> Pocket
COMPONENT P6 — recipe-attached ("Body010", modeled in this document).
Construction recipe (the document's own serialized feature program — sketch geometry with constraints, then the solid features built on it; lengths are millimeters unless a unit is written):

FEATURE [Sketcher::SketchObject] Sketch029
  ArcFitTolerance = 1e-06
  AttachmentSupport = -> [Origin016]
  ExternalTypes = [0]
  FullyConstrained = true
  MakeInternals = false
  MapMode = 5
  Placement = pos=(0,0,0) rot=(0.57735,0.57735,0.57735;2.0944rad)
  _ExternalGeoVersion = 1
  sketch-geometry (5):
    g0: LineSegment StartX=-45 StartY=-7.5 StartZ=0 EndX=45 EndY=-7.5 EndZ=0
    g1: LineSegment StartX=45 StartY=-7.5 StartZ=0 EndX=45 EndY=7.5 EndZ=0
    g2: LineSegment StartX=45 StartY=7.5 StartZ=0 EndX=-45 EndY=7.5 EndZ=0
    g3: LineSegment StartX=-45 StartY=7.5 StartZ=0 EndX=-45 EndY=-7.5 EndZ=0
    g4: GeomPoint [constr] X=0 Y=0 Z=0
  constraints (12):
    c: Coincident(g0,g1)
    c: Coincident(g1,g2)
    c: Coincident(g2,g3)
    c: Coincident(g3,g0)
    c: Horizontal(g0)
    c: Horizontal(g2)
    c: Vertical(g1)
    c: Vertical(g3)
    c: Symmetric(g2,g0,g4)
    c: Distance(g1,g3) = 90
    c: Distance(g0,g2) = 15
    c: Coincident(g4,g-1)
FEATURE [PartDesign::Pad] Pad018
  Direction = (1,0,0)
  Length = 3
  Length2 = 10
  Profile = -> Sketch029
  ReferenceAxis = -> Sketch029 [N_Axis]
  Refine = true
  SideType = 0
  Suppressed = false
  Type = 0
  Type2 = 0
FEATURE [Sketcher::SketchObject] Sketch030
  ArcFitTolerance = 1e-06
  AttachmentSupport = -> [Pad018]
  ExternalGeometry = -> [Pad018]
  ExternalTypes = [0,0]
  FullyConstrained = true
  MakeInternals = false
  MapMode = 5
  Placement = pos=(0,0,0) rot=(0.57735,-0.57735,-0.57735;2.0944rad)
  _ExternalGeoVersion = 1
  sketch-geometry (4):
    g0: Circle CenterX=-11 CenterY=4 CenterZ=0 NormalX=0 NormalY=0 NormalZ=1 AngleXU=0 Radius=1.1
    g1: Circle CenterX=-11 CenterY=-4 CenterZ=0 NormalX=0 NormalY=0 NormalZ=1 AngleXU=0 Radius=1.1
    g2: Circle CenterX=11 CenterY=4 CenterZ=0 NormalX=0 NormalY=0 NormalZ=1 AngleXU=0 Radius=1.1
    g3: Circle CenterX=11 CenterY=-4 CenterZ=0 NormalX=0 NormalY=0 NormalZ=1 AngleXU=0 Radius=1.1
  constraints (12):
    c: Diameter(g0) = 2.2
    c: Equal(g0,g1)
    c: Distance(g0,g1) = 8
    c: Distance(g0,g-2) = 11
    c: Distance(g1,g-2) = 11
    c: Distance(g0,g-1) = 4
    c: Equal(g1,g3)
    c: Equal(g3,g2)
    c: Distance(g3,g-2) = 11
    c: Distance(g2,g-2) = 11
    c: Distance(g2,g-1) = 4
    c: Distance(g2,g3) = 8
FEATURE [PartDesign::Hole] Hole011
  BaseFeature = -> Pad018
  BaseProfileType = 7
  CustomThreadClearance = 0
  Depth = 3
  DepthType = 0
  Diameter = 3.1
  DrillForDepth = false
  DrillPoint = 0
  DrillPointAngle = 118
  HoleCutCountersinkAngle = 90
  HoleCutCustomValues = false
  HoleCutDepth = 2.5
  HoleCutDiameter = 5
  HoleCutType = 2
  ModelThread = false
  Profile = -> Sketch030
  Refine = true
  Suppressed = false
  Tapered = false
  TaperedAngle = 90
  ThreadClass = 0
  ThreadDepth = 3
  ThreadDepthType = 0
  ThreadDiameter = 2.5
  ThreadDirection = 0
  ThreadFit = 2
  ThreadSize = 8
  ThreadType = 1
  Threaded = false
  UseCustomThreadClearance = false
FEATURE [Sketcher::SketchObject] Sketch031
  ArcFitTolerance = 1e-06
  AttachmentSupport = -> [Hole011]
  ExternalTypes = [0]
  FullyConstrained = true
  MakeInternals = false
  MapMode = 5
  Placement = pos=(0,0,0) rot=(0.57735,-0.57735,-0.57735;2.0944rad)
  _ExternalGeoVersion = 1
  sketch-geometry (4):
    g0: LineSegment StartX=-45 StartY=7.5 StartZ=0 EndX=-45 EndY=-7.5 EndZ=0
    g1: LineSegment StartX=-45 StartY=-7.5 StartZ=0 EndX=-35 EndY=-7.5 EndZ=0
    g2: LineSegment StartX=-35 StartY=-7.5 StartZ=0 EndX=-35 EndY=7.5 EndZ=0
    g3: LineSegment StartX=-35 StartY=7.5 StartZ=0 EndX=-45 EndY=7.5 EndZ=0
  constraints (12):
    c: Coincident(g0,g1)
    c: Coincident(g1,g2)
    c: Coincident(g2,g3)
    c: Coincident(g3,g0)
    c: Vertical(g0)
    c: Vertical(g2)
    c: Horizontal(g1)
    c: Horizontal(g3)
    c: Distance(g0,g2) = 10
    c: Distance(g1,g3) = 15
    c: Distance(g-1,g3) = 7.5
    c: Distance(g-2,g0) = 45
FEATURE [PartDesign::Pad] Pad019
  BaseFeature = -> Hole011
  Direction = (-1,0,0)
  Length = 5
  Length2 = 10
  Profile = -> Sketch031
  ReferenceAxis = -> Sketch031 [N_Axis]
  Refine = true
  SideType = 0
  Suppressed = false
  Type = 0
  Type2 = 0
FEATURE [PartDesign::Body] Body004
  AllowCompound = true
  Group = -> [Sketch029,Pad018,Sketch030,Hole011,Sketch031,Pad019]
  Origin = -> Origin016
  Tip = -> Pad019
COMPONENT P7 — same part as P3; its construction recipe is shown at P3.
PROVENANCE & LICENSES
A FreeCAD (.FCStd) document from a public repository crawl; recipes are the document's own serialized feature recipes (and, for linked parts, companion documents' recipes).
License: mit.
